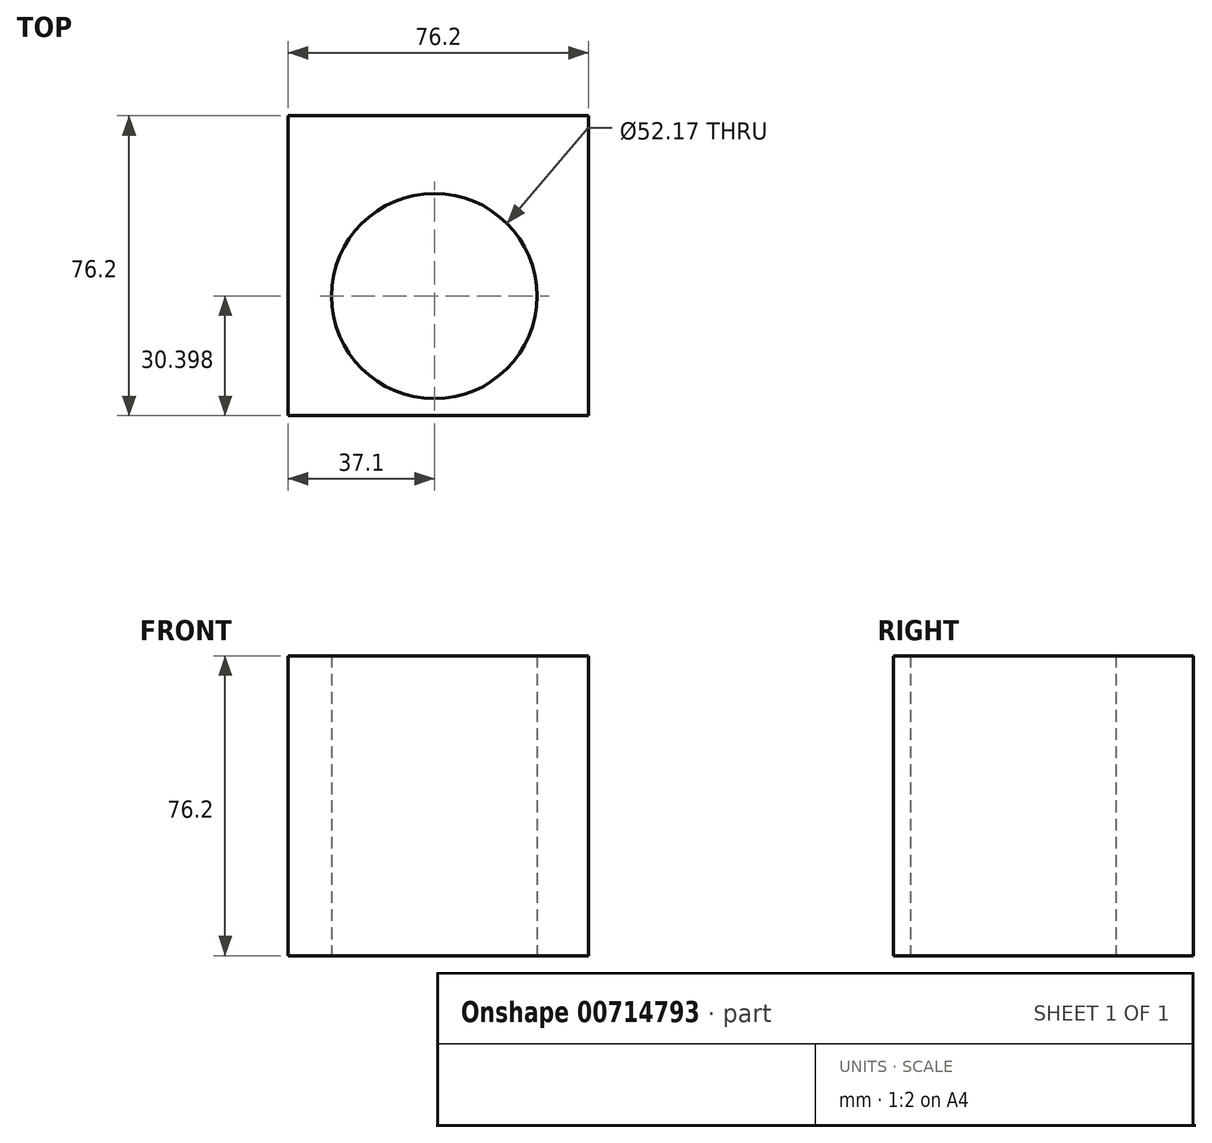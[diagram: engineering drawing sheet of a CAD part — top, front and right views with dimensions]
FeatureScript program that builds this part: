
annotation { "Feature Type Name" : "Feature", "Feature Type Description" : "" }
export const myFeature = defineFeature(function(context is Context, id is Id, definition is map)
    precondition{}
    {
        {
            var Q0;
            Q0=qCreatedBy(makeId("Front.planeOp"),FACE);
            var sketch = newSketch(context, id + "F0", { "sketchPlane" : qUnion([Q0])});
            skLineSegment(sketch, "E0.bottom", {"start": v(-37.1, 25.84) * mm, "end": v(39.1, 25.84) * mm});
            skLineSegment(sketch, "E0.top", {"start": v(-37.1, -50.36) * mm, "end": v(39.1, -50.36) * mm});
            skLineSegment(sketch, "E0.left", {"start": v(-37.1, 25.84) * mm, "end": v(-37.1, -50.36) * mm});
            skLineSegment(sketch, "E0.right", {"start": v(39.1, 25.84) * mm, "end": v(39.1, -50.36) * mm});
            skSolve(sketch);
        }
        {
            var Q0;
            Q0=makeQuery(id+"F0.imprint","IMPRINT",FACE,{"disambiguationData":[TD([[makeQuery(id+"F0.imprint","IMPRINT",EDGE,{"derivedFrom":sQuery(id+"F0.wireOp",EDGE,"E0.bottom")}),-1.0]])]});
            extrude(context, id + "F1", {"entities" : qUnion([Q0]), "depth" : 76.2 * mm, "offsetDistance" : 25.4 * mm});
        }
        {
            var Q0;
            Q0=makeQuery(id+"F1.opExtrude","SWEPT_FACE",FACE,{"disambiguationData":[OSD([sQuery(id+"F0.wireOp",EDGE,"E0.top")])]});
            var sketch = newSketch(context, id + "F2", { "sketchPlane" : qUnion([Q0])});
            skCircle(sketch, "E1", {"center": v(0, 45.8) * mm, "radius": 26.08 * mm});
            skSolve(sketch);
        }
        {
            var Q0;
            Q0 = qSketchRegion(id + "F2", true);
            extrude(context, id + "F3", {"entities" : qUnion([Q0]), "operationType" : NewBodyOperationType.REMOVE, "endBound" : BoundingType.THROUGH_ALL, "oppositeDirection" : true, "depth" : 76.2 * mm, "offsetDistance" : 25.4 * mm});
        }
    });
